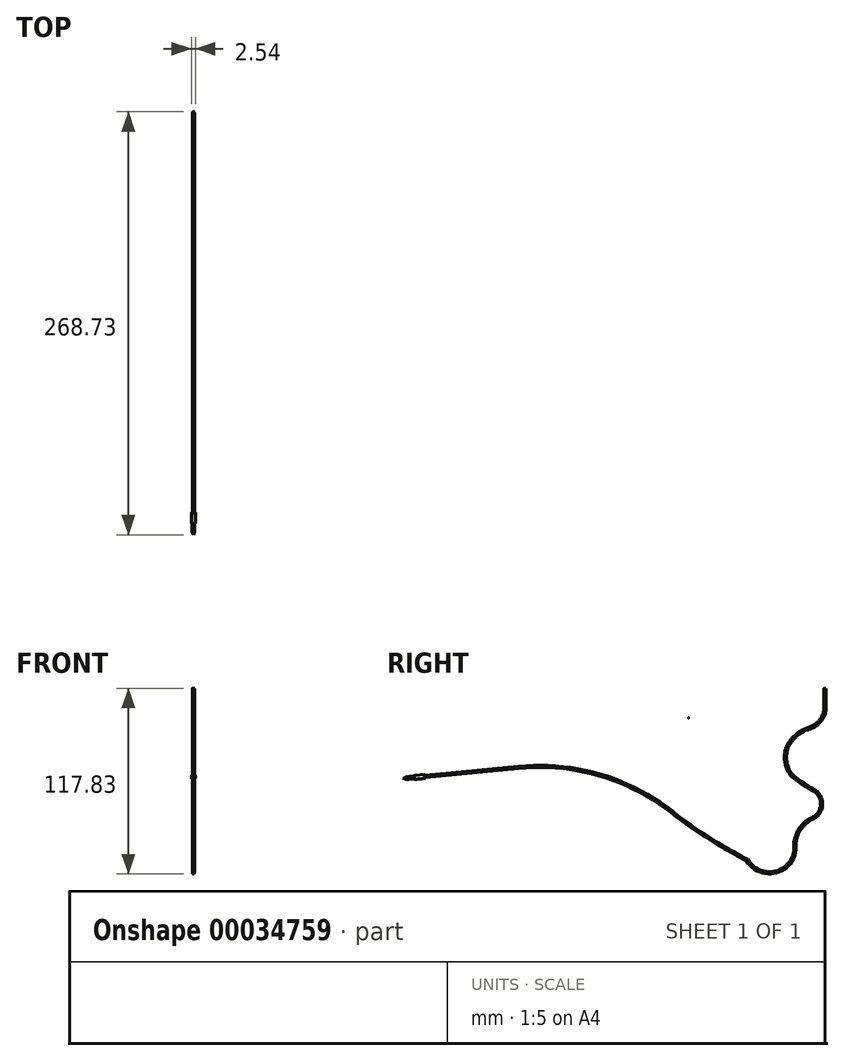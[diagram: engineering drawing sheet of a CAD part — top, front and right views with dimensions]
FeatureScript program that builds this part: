
annotation { "Feature Type Name" : "Feature", "Feature Type Description" : "" }
export const myFeature = defineFeature(function(context is Context, id is Id, definition is map)
    precondition{}
    {
        {
            var Q0;
            Q0=qCreatedBy(makeId("Top.planeOp"),FACE);
            var sketch = newSketch(context, id + "F0", { "sketchPlane" : qUnion([Q0])});
            skCircle(sketch, "E0", {"center": v(0, 0) * mm, "radius": 0.64 * mm});
            skSolve(sketch);
        }
        {
            var Q0;
            Q0=qCreatedBy(makeId("Right.planeOp"),FACE);
            var sketch = newSketch(context, id + "F1", { "sketchPlane" : qUnion([Q0])});
            skLineSegment(sketch, "E1", {"start": v(0, 0) * mm, "end": v(0, -11.85) * mm});
            skArc(sketch, "E2", {"start": v(-10.36, -25.4) * mm, "mid": v(-2.89, -20.37) * mm, "end": v(0, -11.85) * mm});
            skArc(sketch, "E3", {"start": v(-10.36, -25.4) * mm, "mid": v(-18.46, -30.03) * mm, "end": v(-24.12, -37.46) * mm});
            skArc(sketch, "E4", {"start": v(-24.12, -37.46) * mm, "mid": v(-24.93, -46.69) * mm, "end": v(-21.37, -55.24) * mm});
            skArc(sketch, "E5", {"start": v(-21.37, -55.24) * mm, "mid": v(-13.96, -60.62) * mm, "end": v(-6.13, -65.37) * mm});
            skArc(sketch, "E6", {"start": v(-9.2, -83.15) * mm, "mid": v(-2.35, -75.17) * mm, "end": v(-6.13, -65.37) * mm});
            skArc(sketch, "E7", {"start": v(-9.2, -83.15) * mm, "mid": v(-17.12, -91.37) * mm, "end": v(-19.04, -102.62) * mm});
            skArc(sketch, "E8", {"start": v(-93.74, -81.41) * mm, "mid": v(-141.12, -55.67) * mm, "end": v(-194.76, -50.2) * mm});
            skLineSegment(sketch, "E9", {"start": v(-194.76, -50.2) * mm, "end": v(-254, -55.93) * mm});
            skArc(sketch, "E10", {"start": v(-93.74, -81.41) * mm, "mid": v(-72.19, -96.16) * mm, "end": v(-49.53, -109.15) * mm});
            skArc(sketch, "E11", {"start": v(-49.53, -109.15) * mm, "mid": v(-31.94, -116.84) * mm, "end": v(-19.04, -102.62) * mm});
            skSolve(sketch);
        }
        {
            var Q0;
            Q0=makeQuery(id+"F0.imprint","IMPRINT",FACE,{"disambiguationData":[TD([[makeQuery(id+"F0.imprint","IMPRINT",EDGE,{"derivedFrom":sQuery(id+"F0.wireOp",EDGE,"E0")}),1.0]])]});
            var Q1;
            Q1=sQuery(id+"F1.wireOp",EDGE,"E9");
            var Q2;
            Q2=sQuery(id+"F1.wireOp",EDGE,"E8");
            var Q3;
            Q3=sQuery(id+"F1.wireOp",EDGE,"E10");
            var Q4;
            Q4=sQuery(id+"F1.wireOp",EDGE,"E11");
            var Q5;
            Q5=sQuery(id+"F1.wireOp",EDGE,"E7");
            var Q6;
            Q6=sQuery(id+"F1.wireOp",EDGE,"E6");
            var Q7;
            Q7=sQuery(id+"F1.wireOp",EDGE,"E5");
            var Q8;
            Q8=sQuery(id+"F1.wireOp",EDGE,"E4");
            var Q9;
            Q9=sQuery(id+"F1.wireOp",EDGE,"E3");
            var Q10;
            Q10=sQuery(id+"F1.wireOp",EDGE,"E2");
            var Q11;
            Q11=sQuery(id+"F1.wireOp",EDGE,"E1");
            sweep(context, id + "F2", {"profiles" : qUnion([Q0]), "path" : qUnion([Q1, Q2, Q3, Q4, Q5, Q6, Q7, Q8, Q9, Q10, Q11])});
        }
        {
            var Q0;
            Q0=makeQuery(id+"F2.opSweep","CAP_FACE",FACE,{"disambiguationData":[OSD([sQuery(id+"F0.wireOp",EDGE,"E0"),sQuery(id+"F1.wireOp",VERTEX,"E9.end")])],"isStart":false});
            var sketch = newSketch(context, id + "F3", { "sketchPlane" : qUnion([Q0])});
            skCircle(sketch, "E12", {"center": v(0, -31.2) * mm, "radius": 1.27 * mm});
            skSolve(sketch);
        }
        {
            var Q0;
            Q0 = qSketchRegion(id + "F3", true);
            extrude(context, id + "F4", {"entities" : qUnion([Q0]), "operationType" : NewBodyOperationType.ADD, "depth" : 6.8 * mm});
        }
        {
            var Q0;
            Q0=qCreatedBy(makeId("Right.planeOp"),FACE);
            var sketch = newSketch(context, id + "F5", { "sketchPlane" : qUnion([Q0])});
            skLineSegment(sketch, "E13", {"start": v(-86.87, -18.84) * mm, "end": v(-86.53, -18.8) * mm});
            skLineSegment(sketch, "E14", {"start": v(-86.53, -18.8) * mm, "end": v(-86.54, -18.73) * mm});
            skLineSegment(sketch, "E15", {"start": v(-86.54, -18.73) * mm, "end": v(-86.87, -18.84) * mm});
            skSolve(sketch);
        }
        {
            var Q0;
            Q0=makeQuery(id+"F5.imprint","IMPRINT",FACE,{"disambiguationData":[TD([[makeQuery(id+"F5.imprint","IMPRINT",EDGE,{"derivedFrom":sQuery(id+"F5.wireOp",EDGE,"E13")}),1.0]])]});
            var Q1;
            Q1=sQuery(id+"F5.wireOp",EDGE,"E13");
            revolve(context, id + "F6", {"operationType" : NewBodyOperationType.ADD, "entities" : qUnion([Q0]), "axis" : qUnion([Q1]), "revolveType" : RevolveType.FULL});
        }
        {
            var Q0;
            Q0=qCreatedBy(makeId("Right.planeOp"),FACE);
            var sketch = newSketch(context, id + "F7", { "sketchPlane" : qUnion([Q0])});
            skLineSegment(sketch, "E16", {"start": v(-266.1, -57.11) * mm, "end": v(-266, -57.84) * mm});
            skLineSegment(sketch, "E17", {"start": v(-266, -57.84) * mm, "end": v(-268.1, -57.33) * mm});
            skLineSegment(sketch, "E18", {"start": v(-268.1, -57.33) * mm, "end": v(-266.1, -57.11) * mm});
            skLineSegment(sketch, "E19", {"start": v(-266.1, -57.11) * mm, "end": v(-260.77, -56.59) * mm});
            skLineSegment(sketch, "E20", {"start": v(-260.77, -56.59) * mm, "end": v(-260.66, -57.41) * mm});
            skLineSegment(sketch, "E21", {"start": v(-266, -57.84) * mm, "end": v(-260.66, -57.41) * mm, "construction": true});
            skLineSegment(sketch, "E22", {"start": v(-266, -57.84) * mm, "end": v(-265.21, -57.78) * mm});
            skLineSegment(sketch, "E23", {"start": v(-265.21, -57.78) * mm, "end": v(-265.22, -57.65) * mm});
            skLineSegment(sketch, "E24", {"start": v(-265.22, -57.65) * mm, "end": v(-264.88, -57.62) * mm});
            skLineSegment(sketch, "E25", {"start": v(-264.88, -57.62) * mm, "end": v(-264.87, -57.75) * mm});
            skLineSegment(sketch, "E26", {"start": v(-264.87, -57.75) * mm, "end": v(-263.7, -57.66) * mm});
            skLineSegment(sketch, "E27", {"start": v(-263.7, -57.66) * mm, "end": v(-263.71, -57.52) * mm});
            skLineSegment(sketch, "E28", {"start": v(-263.71, -57.52) * mm, "end": v(-263.47, -57.5) * mm});
            skLineSegment(sketch, "E29", {"start": v(-263.47, -57.5) * mm, "end": v(-263.46, -57.64) * mm});
            skLineSegment(sketch, "E30", {"start": v(-263.46, -57.64) * mm, "end": v(-262.16, -57.53) * mm});
            skLineSegment(sketch, "E31", {"start": v(-262.16, -57.53) * mm, "end": v(-262.17, -57.41) * mm});
            skLineSegment(sketch, "E32", {"start": v(-262.17, -57.41) * mm, "end": v(-261.94, -57.4) * mm});
            skLineSegment(sketch, "E33", {"start": v(-261.94, -57.4) * mm, "end": v(-261.93, -57.51) * mm});
            skLineSegment(sketch, "E34", {"start": v(-261.93, -57.51) * mm, "end": v(-260.66, -57.41) * mm});
            skSolve(sketch);
        }
        {
            var Q0;
            Q0 = qSketchRegion(id + "F7", true);
            var Q1;
            Q1=sQuery(id+"F7.wireOp",EDGE,"E18");
            revolve(context, id + "F8", {"operationType" : NewBodyOperationType.ADD, "entities" : qUnion([Q0]), "axis" : qUnion([Q1]), "revolveType" : RevolveType.FULL});
        }
    });
